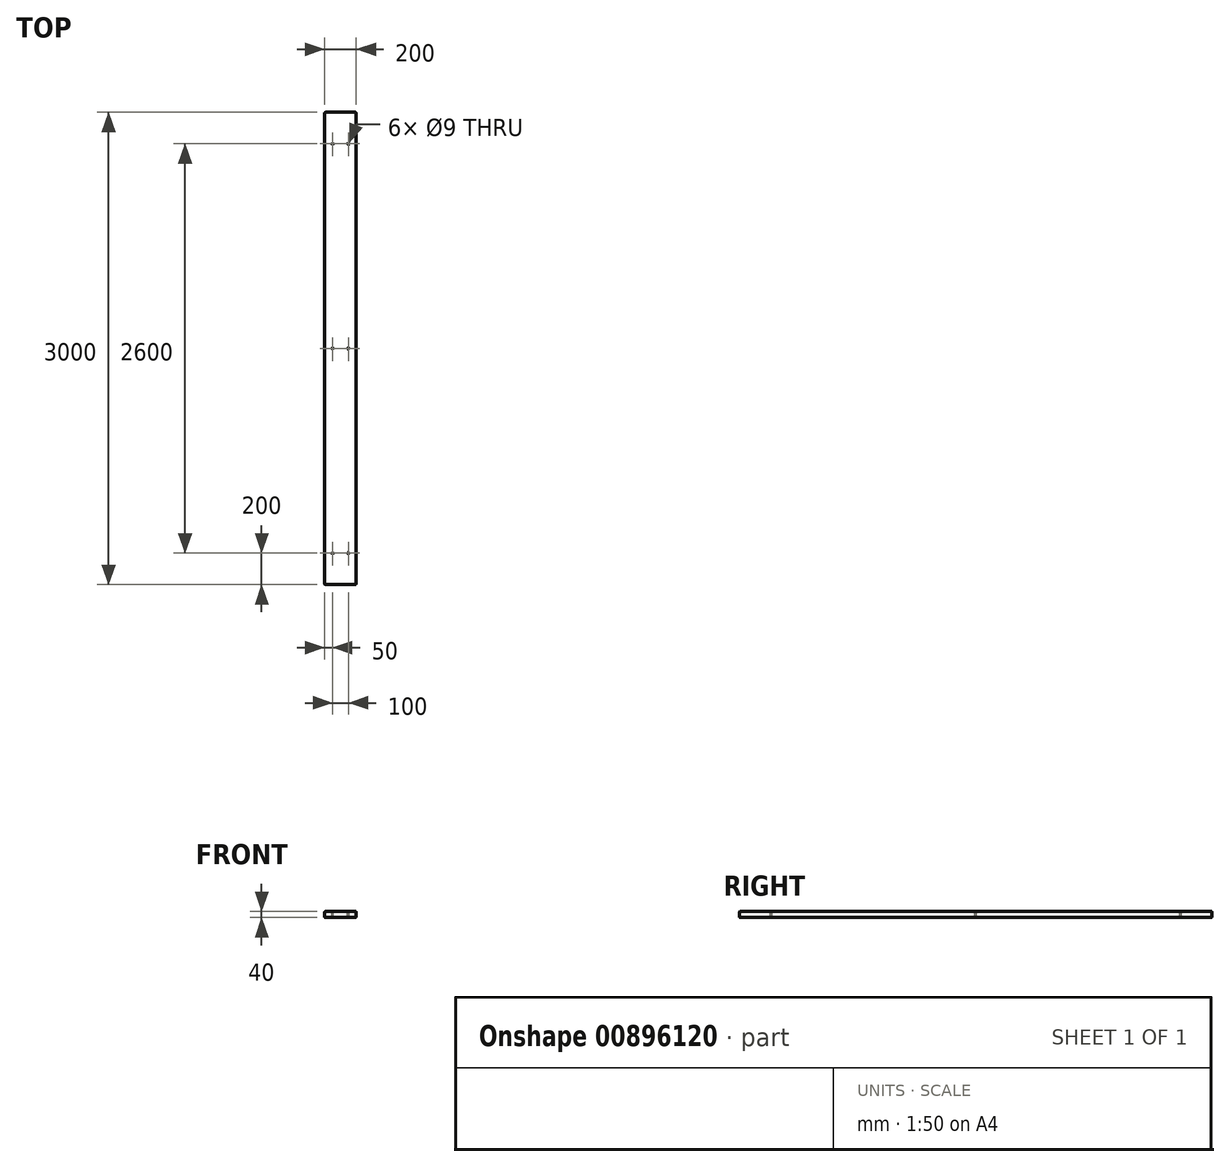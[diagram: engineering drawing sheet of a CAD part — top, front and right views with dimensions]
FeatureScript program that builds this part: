
annotation { "Feature Type Name" : "Feature", "Feature Type Description" : "" }
export const myFeature = defineFeature(function(context is Context, id is Id, definition is map)
    precondition{}
    {
        {
            var Q0;
            Q0=qCreatedBy(makeId("Front.planeOp"),FACE);
            var sketch = newSketch(context, id + "F0", { "sketchPlane" : qUnion([Q0])});
            skLineSegment(sketch, "E0.bottom", {"start": v(0, 0) * mm, "end": v(200, 0) * mm});
            skLineSegment(sketch, "E0.top", {"start": v(0, 40) * mm, "end": v(200, 40) * mm});
            skLineSegment(sketch, "E0.left", {"start": v(0, 0) * mm, "end": v(0, 40) * mm});
            skLineSegment(sketch, "E0.right", {"start": v(200, 0) * mm, "end": v(200, 40) * mm});
            skSolve(sketch);
        }
        {
            var Q0;
            Q0 = qSketchRegion(id + "F0", true);
            extrude(context, id + "F1", {"entities" : qUnion([Q0]), "depth" : 3000 * mm, "offsetDistance" : 25 * mm});
        }
        {
            var Q0;
            Q0=makeQuery(id+"F1.opExtrude","SWEPT_FACE",FACE,{"disambiguationData":[OSD([sQuery(id+"F0.wireOp",EDGE,"E0.top")])]});
            var sketch = newSketch(context, id + "F2", { "sketchPlane" : qUnion([Q0])});
            skLineSegment(sketch, "E1", {"start": v(0, -3000) * mm, "end": v(50, -3000) * mm, "construction": true});
            skLineSegment(sketch, "E2", {"start": v(50, -3000) * mm, "end": v(150, -3000) * mm, "construction": true});
            skLineSegment(sketch, "E3", {"start": v(150, -3000) * mm, "end": v(200, -3000) * mm, "construction": true});
            skLineSegment(sketch, "E4", {"start": v(50, -3000) * mm, "end": v(50, -2800) * mm, "construction": true});
            skLineSegment(sketch, "E5", {"start": v(50, -2800) * mm, "end": v(50, -200) * mm, "construction": true});
            skLineSegment(sketch, "E6", {"start": v(50, -200) * mm, "end": v(50, 0) * mm, "construction": true});
            skLineSegment(sketch, "E7", {"start": v(150, -3000) * mm, "end": v(150, -2800) * mm, "construction": true});
            skLineSegment(sketch, "E8", {"start": v(150, -2800) * mm, "end": v(150, -200) * mm, "construction": true});
            skLineSegment(sketch, "E9", {"start": v(150, -200) * mm, "end": v(150, 0) * mm, "construction": true});
            skCircle(sketch, "E10", {"center": v(50, -2800) * mm, "radius": 4.5 * mm});
            skCircle(sketch, "E11", {"center": v(150, -2800) * mm, "radius": 4.5 * mm});
            skCircle(sketch, "E12", {"center": v(50, -200) * mm, "radius": 4.5 * mm});
            skCircle(sketch, "E13", {"center": v(150, -200) * mm, "radius": 4.5 * mm});
            skPoint(sketch, "E14", {"position": v(50, -1500) * mm});
            skPoint(sketch, "E15", {"position": v(150, -1500) * mm});
            skCircle(sketch, "E16", {"center": v(50, -1500) * mm, "radius": 4.5 * mm});
            skCircle(sketch, "E17", {"center": v(150, -1500) * mm, "radius": 4.5 * mm});
            skSolve(sketch);
        }
        {
            var Q0;
            Q0 = qSketchRegion(id + "F2", true);
            extrude(context, id + "F3", {"entities" : qUnion([Q0]), "operationType" : NewBodyOperationType.REMOVE, "endBound" : BoundingType.THROUGH_ALL, "oppositeDirection" : true, "depth" : 25 * mm, "offsetDistance" : 25 * mm});
        }
        {
            var Q0;
            Q0=makeQuery(id+"F1.opExtrude","SWEPT_EDGE",EDGE,{"disambiguationData":[OSD([sQuery(id+"F0.wireOp",EDGE,"E0.top"),sQuery(id+"F0.wireOp",EDGE,"E0.left")])]});
            var Q1;
            Q1=makeQuery(id+"F1.opExtrude","SWEPT_EDGE",EDGE,{"disambiguationData":[OSD([sQuery(id+"F0.wireOp",EDGE,"E0.bottom"),sQuery(id+"F0.wireOp",EDGE,"E0.left")])]});
            var Q2;
            Q2=makeQuery(id+"F1.opExtrude","SWEPT_EDGE",EDGE,{"disambiguationData":[OSD([sQuery(id+"F0.wireOp",EDGE,"E0.top"),sQuery(id+"F0.wireOp",EDGE,"E0.right")])]});
            var Q3;
            Q3=makeQuery(id+"F1.opExtrude","SWEPT_EDGE",EDGE,{"disambiguationData":[OSD([sQuery(id+"F0.wireOp",EDGE,"E0.bottom"),sQuery(id+"F0.wireOp",EDGE,"E0.right")])]});
            var Q4;
            Q4=makeQuery(id+"F1.opExtrude","CAP_EDGE",EDGE,{"disambiguationData":[OSD([sQuery(id+"F0.wireOp",EDGE,"E0.top")])],"isStart":false});
            var Q5;
            Q5=makeQuery(id+"F1.opExtrude","CAP_EDGE",EDGE,{"disambiguationData":[OSD([sQuery(id+"F0.wireOp",EDGE,"E0.bottom")])],"isStart":false});
            var Q6;
            Q6=makeQuery(id+"F1.opExtrude","CAP_EDGE",EDGE,{"disambiguationData":[OSD([sQuery(id+"F0.wireOp",EDGE,"E0.left")])],"isStart":false});
            var Q7;
            Q7=makeQuery(id+"F1.opExtrude","CAP_EDGE",EDGE,{"disambiguationData":[OSD([sQuery(id+"F0.wireOp",EDGE,"E0.right")])],"isStart":false});
            var Q8;
            Q8=makeQuery(id+"F1.opExtrude","CAP_EDGE",EDGE,{"disambiguationData":[OSD([sQuery(id+"F0.wireOp",EDGE,"E0.right")])],"isStart":true});
            var Q9;
            Q9=makeQuery(id+"F1.opExtrude","CAP_EDGE",EDGE,{"disambiguationData":[OSD([sQuery(id+"F0.wireOp",EDGE,"E0.top")])],"isStart":true});
            var Q10;
            Q10=makeQuery(id+"F1.opExtrude","CAP_EDGE",EDGE,{"disambiguationData":[OSD([sQuery(id+"F0.wireOp",EDGE,"E0.bottom")])],"isStart":true});
            var Q11;
            Q11=makeQuery(id+"F1.opExtrude","CAP_EDGE",EDGE,{"disambiguationData":[OSD([sQuery(id+"F0.wireOp",EDGE,"E0.left")])],"isStart":true});
            fillet(context, id + "F4", {"entities" : qUnion([Q0, Q1, Q2, Q3, Q4, Q5, Q6, Q7, Q8, Q9, Q10, Q11]), "radius" : 5 * mm, "tangentPropagation" : true, "allowEdgeOverflow" : false});
        }
    });
